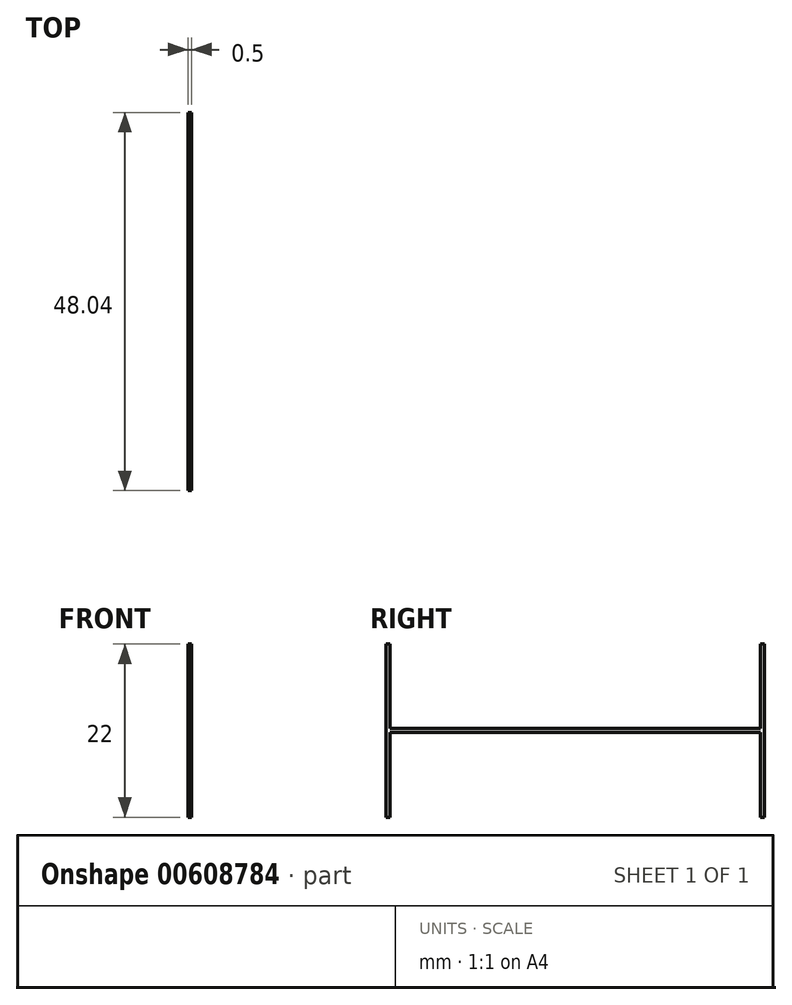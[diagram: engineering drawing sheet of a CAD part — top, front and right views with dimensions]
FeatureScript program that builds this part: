
annotation { "Feature Type Name" : "Feature", "Feature Type Description" : "" }
export const myFeature = defineFeature(function(context is Context, id is Id, definition is map)
    precondition{}
    {
        {
            var Q0;
            Q0=qCreatedBy(makeId("Right.planeOp"),FACE);
            var sketch = newSketch(context, id + "F0", { "sketchPlane" : qUnion([Q0])});
            skLineSegment(sketch, "E0", {"start": v(0, 11) * mm, "end": v(-0.5, 11) * mm});
            skLineSegment(sketch, "E1", {"start": v(-0.5, 11) * mm, "end": v(-0.5, -11) * mm});
            skLineSegment(sketch, "E2", {"start": v(-0.5, -11) * mm, "end": v(0, -11) * mm});
            skLineSegment(sketch, "E3", {"start": v(47.04, 11) * mm, "end": v(47.54, 11) * mm});
            skLineSegment(sketch, "E4", {"start": v(47.54, 11) * mm, "end": v(47.54, -11) * mm});
            skLineSegment(sketch, "E5", {"start": v(47.54, -11) * mm, "end": v(47.04, -11) * mm});
            skLineSegment(sketch, "E6.0", {"start": v(0, -0.25) * mm, "end": v(47.04, -0.25) * mm});
            skLineSegment(sketch, "E7.0", {"start": v(0, 0.25) * mm, "end": v(47.04, 0.25) * mm});
            skLineSegment(sketch, "E8", {"start": v(47.04, 11) * mm, "end": v(47.04, 0.25) * mm});
            skLineSegment(sketch, "E9", {"start": v(47.04, -0.25) * mm, "end": v(47.04, -11) * mm});
            skLineSegment(sketch, "E10", {"start": v(0, 11) * mm, "end": v(0, 0.25) * mm});
            skLineSegment(sketch, "E11", {"start": v(0, -0.25) * mm, "end": v(0, -11) * mm});
            skSolve(sketch);
        }
        {
            var Q0;
            Q0=makeQuery(id+"F0.imprint","IMPRINT",FACE,{"disambiguationData":[TD([[makeQuery(id+"F0.imprint","IMPRINT",EDGE,{"derivedFrom":sQuery(id+"F0.wireOp",EDGE,"E0")}),1.0]])]});
            extrude(context, id + "F1", {"entities" : qUnion([Q0]), "depth" : .5 * mm, "offsetDistance" : 25 * mm});
        }
    });
